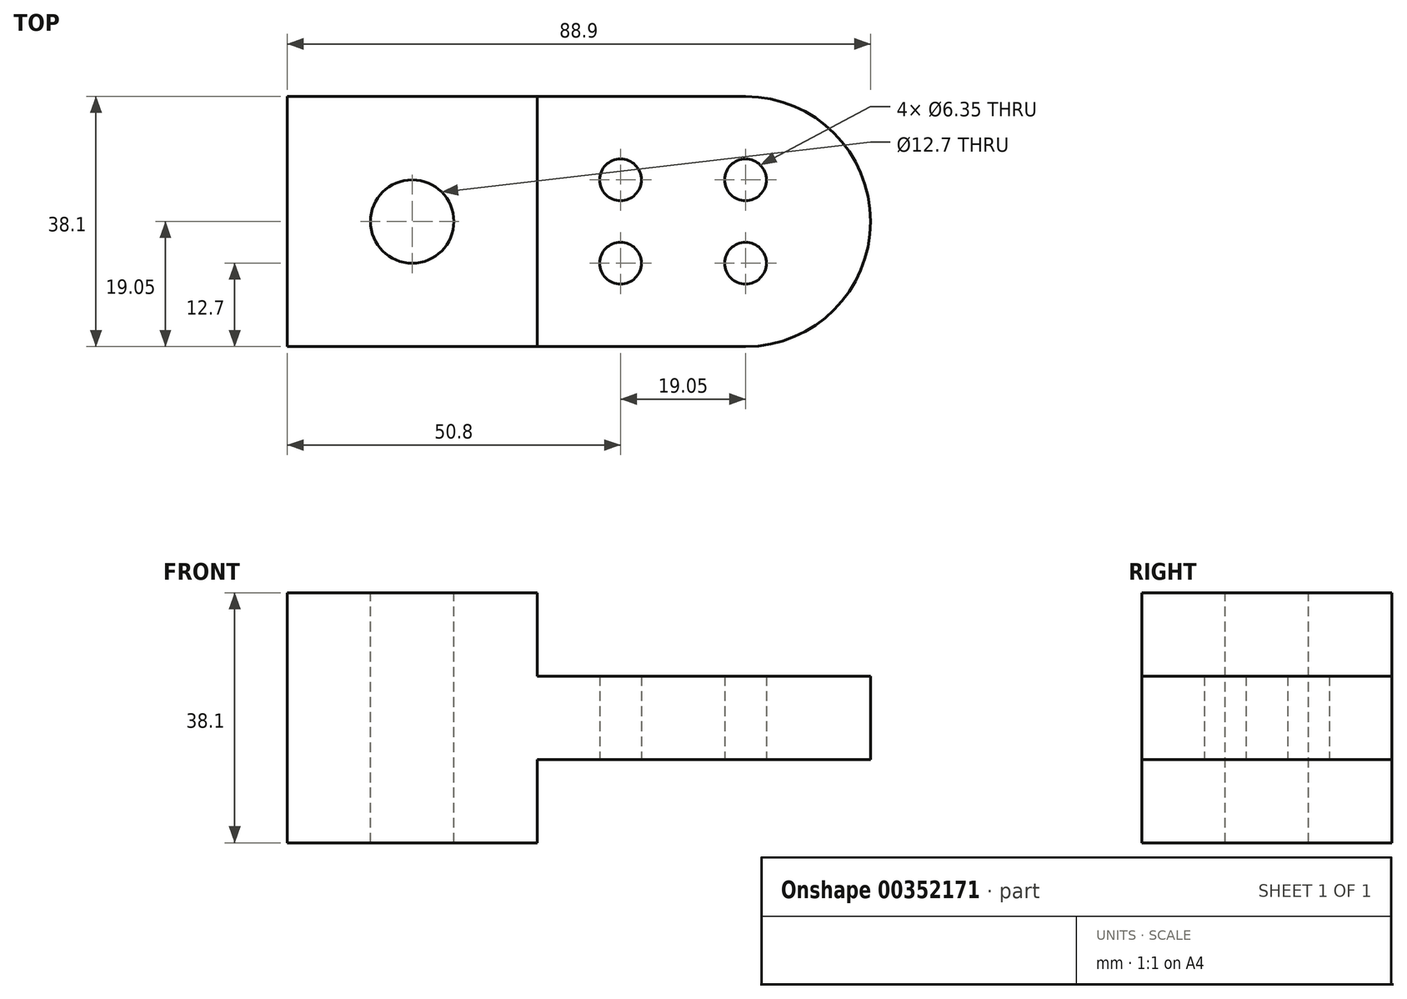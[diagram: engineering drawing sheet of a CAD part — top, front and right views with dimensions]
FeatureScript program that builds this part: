
annotation { "Feature Type Name" : "Feature", "Feature Type Description" : "" }
export const myFeature = defineFeature(function(context is Context, id is Id, definition is map)
    precondition{}
    {
        {
            var Q0;
            Q0=qCreatedBy(makeId("Top.planeOp"),FACE);
            var sketch = newSketch(context, id + "F0", { "sketchPlane" : qUnion([Q0])});
            skLineSegment(sketch, "E0", {"start": v(0, 0) * mm, "end": v(0, -38.1) * mm});
            skLineSegment(sketch, "E1", {"start": v(0, 0) * mm, "end": v(31.75, 0) * mm});
            skLineSegment(sketch, "E2", {"start": v(0, -38.1) * mm, "end": v(31.75, -38.1) * mm});
            skArc(sketch, "E3", {"start": v(31.75, 0) * mm, "mid": v(50.8, -19.05) * mm, "end": v(31.75, -38.1) * mm});
            skLineSegment(sketch, "E4.bottom", {"start": v(12.7, -12.7) * mm, "end": v(31.75, -12.7) * mm, "construction": true});
            skLineSegment(sketch, "E4.top", {"start": v(12.7, -25.4) * mm, "end": v(31.75, -25.4) * mm, "construction": true});
            skLineSegment(sketch, "E4.left", {"start": v(12.7, -12.7) * mm, "end": v(12.7, -25.4) * mm, "construction": true});
            skLineSegment(sketch, "E4.right", {"start": v(31.75, -12.7) * mm, "end": v(31.75, -25.4) * mm, "construction": true});
            skLineSegment(sketch, "E5", {"start": v(31.75, -19.05) * mm, "end": v(-56.06, -19.05) * mm, "construction": true});
            skCircle(sketch, "E6", {"center": v(12.7, -12.7) * mm, "radius": 3.18 * mm});
            skCircle(sketch, "E7", {"center": v(31.75, -12.7) * mm, "radius": 3.18 * mm});
            skCircle(sketch, "E8", {"center": v(31.75, -25.4) * mm, "radius": 3.18 * mm});
            skCircle(sketch, "E9", {"center": v(12.7, -25.4) * mm, "radius": 3.18 * mm});
            skSolve(sketch);
        }
        {
            var Q0;
            Q0=makeQuery(id+"F0.imprint","IMPRINT",FACE,{"disambiguationData":[TD([[makeQuery(id+"F0.imprint","IMPRINT",EDGE,{"derivedFrom":sQuery(id+"F0.wireOp",EDGE,"E0")}),1.0]])]});
            extrude(context, id + "F1", {"entities" : qUnion([Q0]), "depth" : 12.7 * mm});
        }
        {
            var Q0;
            Q0=makeQuery(id+"F1.opExtrude","SWEPT_FACE",FACE,{"disambiguationData":[OSD([sQuery(id+"F0.wireOp",EDGE,"E2")])]});
            var sketch = newSketch(context, id + "F2", { "sketchPlane" : qUnion([Q0])});
            skLineSegment(sketch, "E10", {"start": v(0, 0) * mm, "end": v(0, -12.7) * mm});
            skLineSegment(sketch, "E11", {"start": v(0, -12.7) * mm, "end": v(-38.1, -12.7) * mm});
            skLineSegment(sketch, "E12", {"start": v(-38.1, -12.7) * mm, "end": v(-38.1, 25.4) * mm});
            skLineSegment(sketch, "E13", {"start": v(-38.1, 25.4) * mm, "end": v(0, 25.4) * mm});
            skLineSegment(sketch, "E14", {"start": v(0, 25.4) * mm, "end": v(0, 0) * mm});
            skSolve(sketch);
        }
        {
            var Q0;
            {var subQ1=sQuery(id+"F2.wireOp",EDGE,"E10");Q0=makeQuery(id+"F2.imprint","IMPRINT",FACE,{"disambiguationData":[TD([[makeQuery(id+"F2.imprint","IMPRINT",EDGE,{"derivedFrom":subQ1}),-1.0]])]});}
            extrude(context, id + "F3", {"entities" : qUnion([Q0]), "operationType" : NewBodyOperationType.ADD, "oppositeDirection" : true, "depth" : 38.1 * mm});
        }
        {
            var Q0;
            Q0=makeQuery(id+"F3.opExtrude","SWEPT_FACE",FACE,{"disambiguationData":[OSD([sQuery(id+"F2.wireOp",EDGE,"E13")])]});
            var sketch = newSketch(context, id + "F4", { "sketchPlane" : qUnion([Q0])});
            skCircle(sketch, "E15", {"center": v(-19.05, -19.05) * mm, "radius": 6.35 * mm});
            skSolve(sketch);
        }
        {
            var Q0;
            Q0=makeQuery(id+"F4.imprint","IMPRINT",FACE,{"disambiguationData":[TD([[makeQuery(id+"F4.imprint","IMPRINT",EDGE,{"derivedFrom":sQuery(id+"F4.wireOp",EDGE,"E15")}),1.0]])]});
            extrude(context, id + "F5", {"entities" : qUnion([Q0]), "operationType" : NewBodyOperationType.REMOVE, "endBound" : BoundingType.THROUGH_ALL, "oppositeDirection" : true, "depth" : 25.4 * mm});
        }
    });
